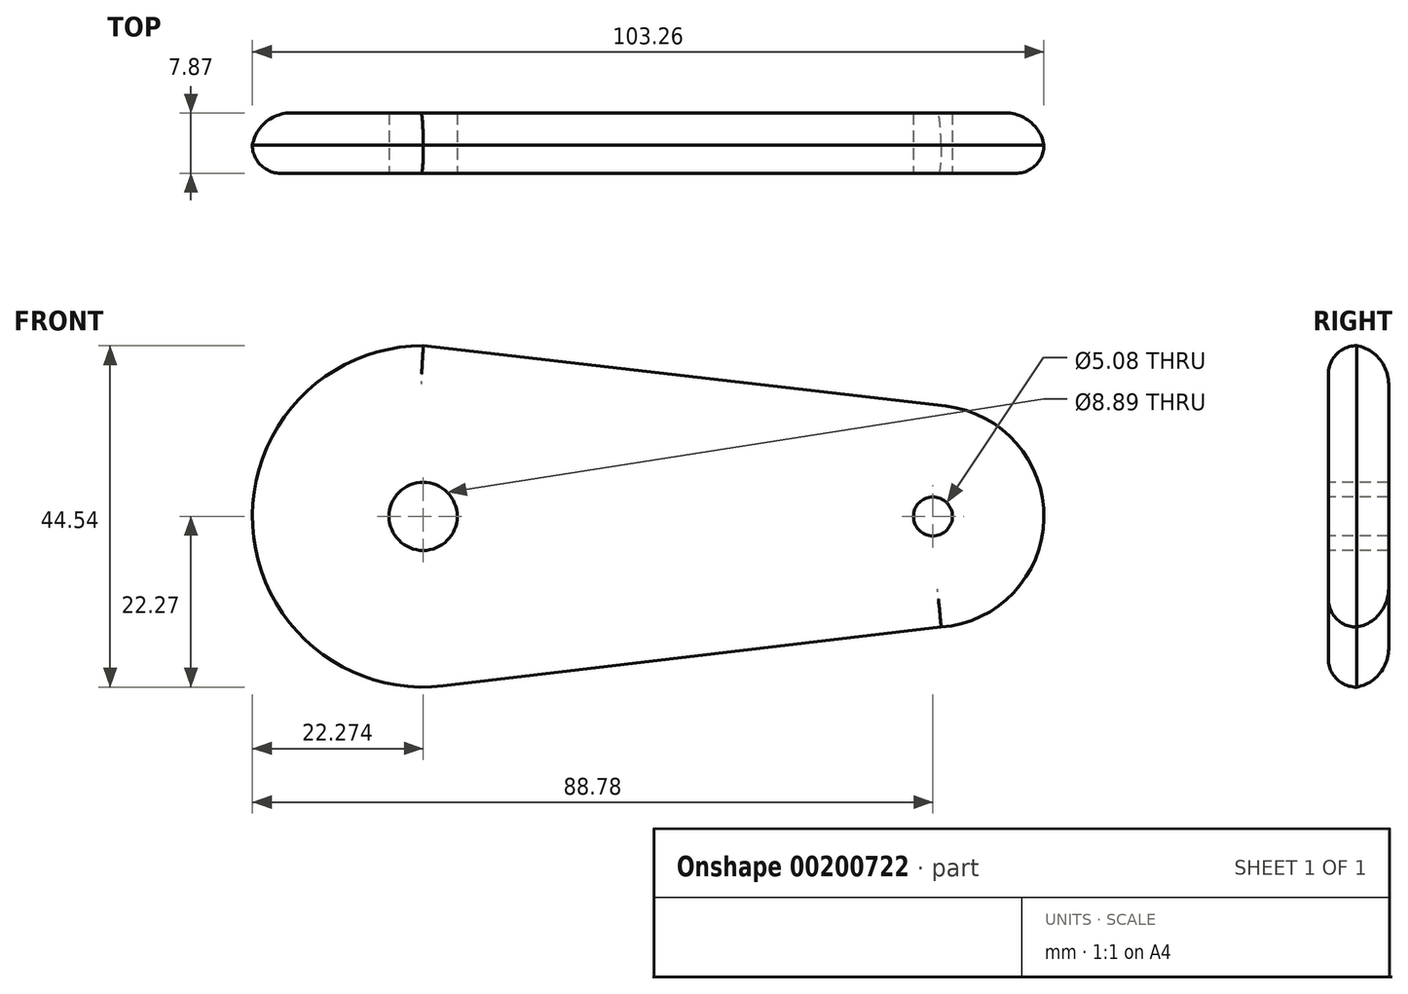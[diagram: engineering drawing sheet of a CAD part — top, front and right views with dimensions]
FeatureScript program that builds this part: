
annotation { "Feature Type Name" : "Feature", "Feature Type Description" : "" }
export const myFeature = defineFeature(function(context is Context, id is Id, definition is map)
    precondition{}
    {
        {
            var Q0;
            Q0=qCreatedBy(makeId("Front.planeOp"),FACE);
            var sketch = newSketch(context, id + "F0", { "sketchPlane" : qUnion([Q0])});
            skArc(sketch, "E0", {"start": v(-30.45, 21.69) * mm, "mid": v(-57.75, 1.25) * mm, "end": v(-32.9, -22.12) * mm});
            skArc(sketch, "E1", {"start": v(32.06, -14.44) * mm, "mid": v(45.47, -0.3) * mm, "end": v(32.65, 14.39) * mm});
            skLineSegment(sketch, "E2", {"start": v(-35.5, 22.27) * mm, "end": v(32.65, 14.39) * mm});
            skLineSegment(sketch, "E3", {"start": v(32.06, -14.44) * mm, "end": v(-32.9, -22.12) * mm});
            skSolve(sketch);
        }
        {
            var Q0;
            {var subQ3=sQuery(id+"F0.wireOp",EDGE,"E1");Q0=makeQuery(id+"F0.imprint","IMPRINT",FACE,{"disambiguationData":[TD([[makeQuery(id+"F0.imprint","IMPRINT",EDGE,{"derivedFrom":subQ3}),1.0]])]});}
            extrude(context, id + "F1", {"entities" : qUnion([Q0]), "oppositeDirection" : true, "depth" : 7.87 * mm});
        }
        {
            var Q0;
            Q0=makeQuery(id+"F1.opExtrude","CAP_FACE",FACE,{"disambiguationData":[OSD([sQuery(id+"F0.wireOp",EDGE,"E0"),sQuery(id+"F0.wireOp",EDGE,"E1"),sQuery(id+"F0.wireOp",EDGE,"E2"),sQuery(id+"F0.wireOp",EDGE,"E3")])],"isStart":true});
            fillet(context, id + "F2", {"entities" : qUnion([Q0]), "radius" : 3.68 * mm, "tangentPropagation" : true, "allowEdgeOverflow" : false});
        }
        {
            var Q0;
            Q0=makeQuery(id+"F1.opExtrude","CAP_FACE",FACE,{"disambiguationData":[OSD([sQuery(id+"F0.wireOp",EDGE,"E0"),sQuery(id+"F0.wireOp",EDGE,"E1"),sQuery(id+"F0.wireOp",EDGE,"E2"),sQuery(id+"F0.wireOp",EDGE,"E3")])],"isStart":false});
            fillet(context, id + "F3", {"entities" : qUnion([Q0]), "radius" : 5.08 * mm, "tangentPropagation" : true, "allowEdgeOverflow" : false});
        }
        {
            var Q0;
            Q0=sQuery(id+"F0.wireOp",VERTEX,"E1.center");
            var Q1;
            Q1=makeQuery(id+"F1.opExtrude","SWEPT_BODY",BODY,{"disambiguationData":[OSD([sQuery(id+"F0.wireOp",EDGE,"E0"),sQuery(id+"F0.wireOp",EDGE,"E1"),sQuery(id+"F0.wireOp",EDGE,"E2"),sQuery(id+"F0.wireOp",EDGE,"E3")])]});
            hole(context, id + "F4", {"style" : HoleStyle.SIMPLE, "endStyle" : HoleEndStyle.THROUGH, "holeDiameter" : 5.08 * mm, "locations" : qUnion([Q0]), "scope" : qUnion([Q1]), "isTappedThrough" : true});
        }
        {
            var Q0;
            Q0=sQuery(id+"F0.wireOp",VERTEX,"E0.center");
            var Q1;
            Q1=makeQuery(id+"F1.opExtrude","SWEPT_BODY",BODY,{"disambiguationData":[OSD([sQuery(id+"F0.wireOp",EDGE,"E0"),sQuery(id+"F0.wireOp",EDGE,"E1"),sQuery(id+"F0.wireOp",EDGE,"E2"),sQuery(id+"F0.wireOp",EDGE,"E3")])]});
            hole(context, id + "F5", {"style" : HoleStyle.SIMPLE, "endStyle" : HoleEndStyle.THROUGH, "holeDiameter" : 8.9 * mm, "locations" : qUnion([Q0]), "scope" : qUnion([Q1]), "isTappedThrough" : true});
        }
    });
